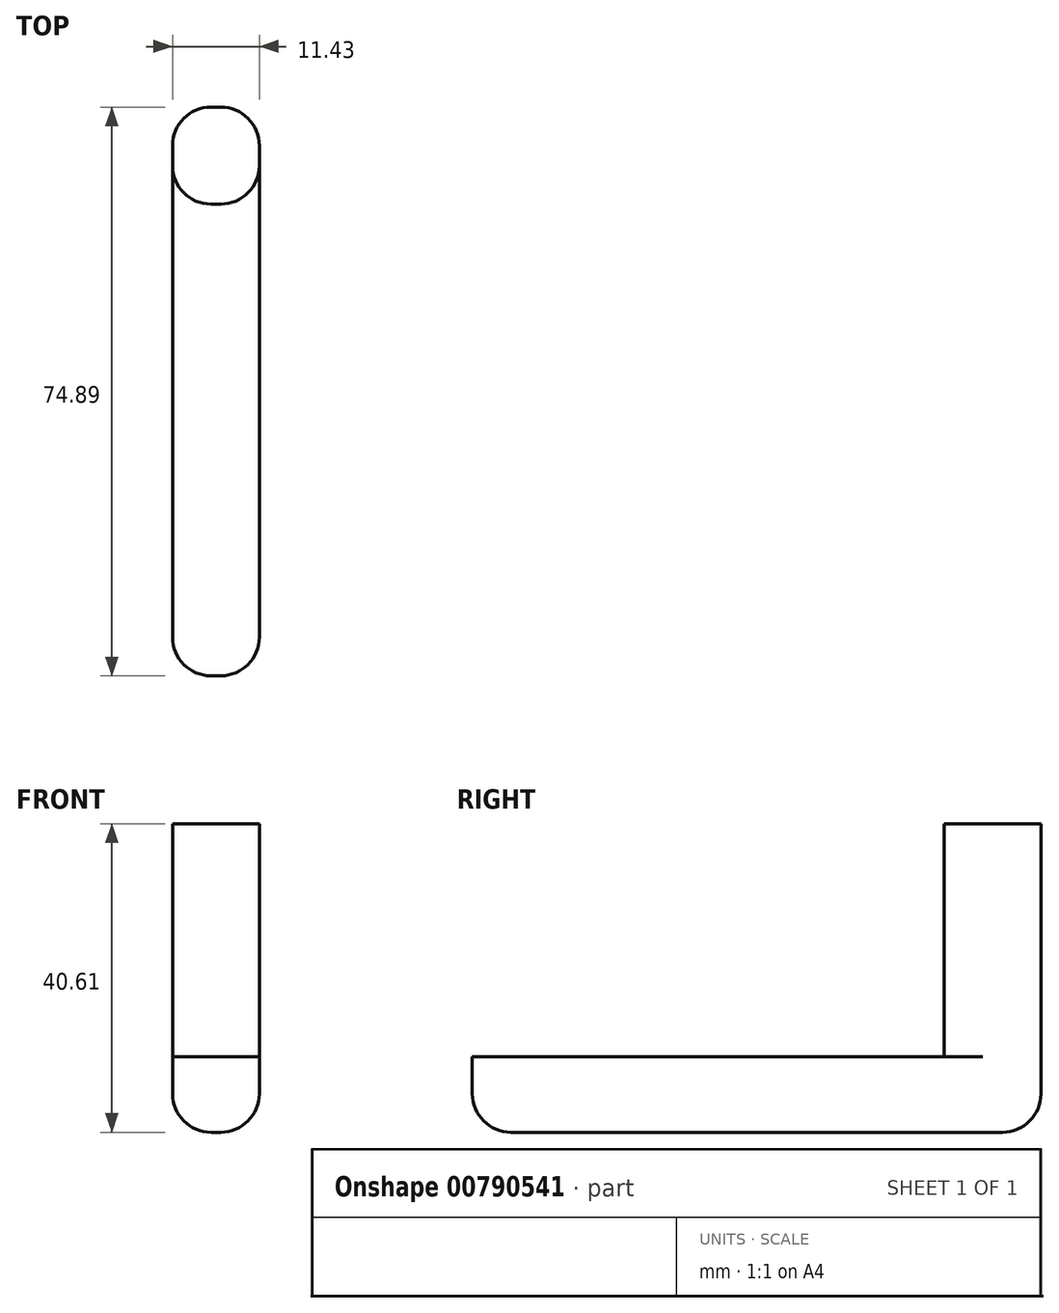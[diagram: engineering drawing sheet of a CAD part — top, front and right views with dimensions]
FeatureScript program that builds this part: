
annotation { "Feature Type Name" : "Feature", "Feature Type Description" : "" }
export const myFeature = defineFeature(function(context is Context, id is Id, definition is map)
    precondition{}
    {
        {
            var Q0;
            Q0=qCreatedBy(makeId("Right.planeOp"),FACE);
            var sketch = newSketch(context, id + "F0", { "sketchPlane" : qUnion([Q0])});
            skLineSegment(sketch, "E0", {"start": v(-62.11, 14.59) * mm, "end": v(0, 14.59) * mm});
            skLineSegment(sketch, "E1", {"start": v(0, 14.59) * mm, "end": v(0, 45.27) * mm});
            skLineSegment(sketch, "E2", {"start": v(0, 45.27) * mm, "end": v(12.78, 45.27) * mm});
            skLineSegment(sketch, "E3", {"start": v(12.78, 45.27) * mm, "end": v(12.78, 4.66) * mm});
            skLineSegment(sketch, "E4", {"start": v(12.78, 4.66) * mm, "end": v(-62.11, 4.66) * mm});
            skLineSegment(sketch, "E5", {"start": v(-62.11, 4.66) * mm, "end": v(-62.11, 14.59) * mm});
            skSolve(sketch);
        }
        {
            var Q0;
            Q0 = qSketchRegion(id + "F0", true);
            extrude(context, id + "F1", {"entities" : qUnion([Q0]), "depth" : 11.43 * mm, "offsetDistance" : 25.4 * mm});
        }
        {
            var Q0;
            Q0=makeQuery(id+"F1.opExtrude","CAP_EDGE",EDGE,{"disambiguationData":[OSD([sQuery(id+"F0.wireOp",EDGE,"E1")])],"isStart":false});
            var Q1;
            Q1=makeQuery(id+"F1.opExtrude","CAP_EDGE",EDGE,{"disambiguationData":[OSD([sQuery(id+"F0.wireOp",EDGE,"E1")])],"isStart":true});
            var Q2;
            Q2=makeQuery(id+"F1.opExtrude","CAP_EDGE",EDGE,{"disambiguationData":[OSD([sQuery(id+"F0.wireOp",EDGE,"E3")])],"isStart":false});
            var Q3;
            Q3=makeQuery(id+"F1.opExtrude","CAP_EDGE",EDGE,{"disambiguationData":[OSD([sQuery(id+"F0.wireOp",EDGE,"E4")])],"isStart":false});
            var Q4;
            Q4=makeQuery(id+"F1.opExtrude","CAP_EDGE",EDGE,{"disambiguationData":[OSD([sQuery(id+"F0.wireOp",EDGE,"E4")])],"isStart":true});
            var Q5;
            Q5=makeQuery(id+"F1.opExtrude","CAP_EDGE",EDGE,{"disambiguationData":[OSD([sQuery(id+"F0.wireOp",EDGE,"E3")])],"isStart":true});
            var Q6;
            Q6=makeQuery(id+"F1.opExtrude","CAP_EDGE",EDGE,{"disambiguationData":[OSD([sQuery(id+"F0.wireOp",EDGE,"E5")])],"isStart":true});
            var Q7;
            Q7=makeQuery(id+"F1.opExtrude","CAP_EDGE",EDGE,{"disambiguationData":[OSD([sQuery(id+"F0.wireOp",EDGE,"E5")])],"isStart":false});
            var Q8;
            Q8=makeQuery(id+"F1.opExtrude","SWEPT_EDGE",EDGE,{"disambiguationData":[OSD([sQuery(id+"F0.wireOp",EDGE,"E4"),sQuery(id+"F0.wireOp",EDGE,"E5")])]});
            var Q9;
            Q9=makeQuery(id+"F1.opExtrude","SWEPT_EDGE",EDGE,{"disambiguationData":[OSD([sQuery(id+"F0.wireOp",EDGE,"E3"),sQuery(id+"F0.wireOp",EDGE,"E4")])]});
            fillet(context, id + "F2", {"entities" : qUnion([Q0, Q1, Q2, Q3, Q4, Q5, Q6, Q7, Q8, Q9]), "radius" : 5.08 * mm, "tangentPropagation" : true, "allowEdgeOverflow" : false});
        }
    });
